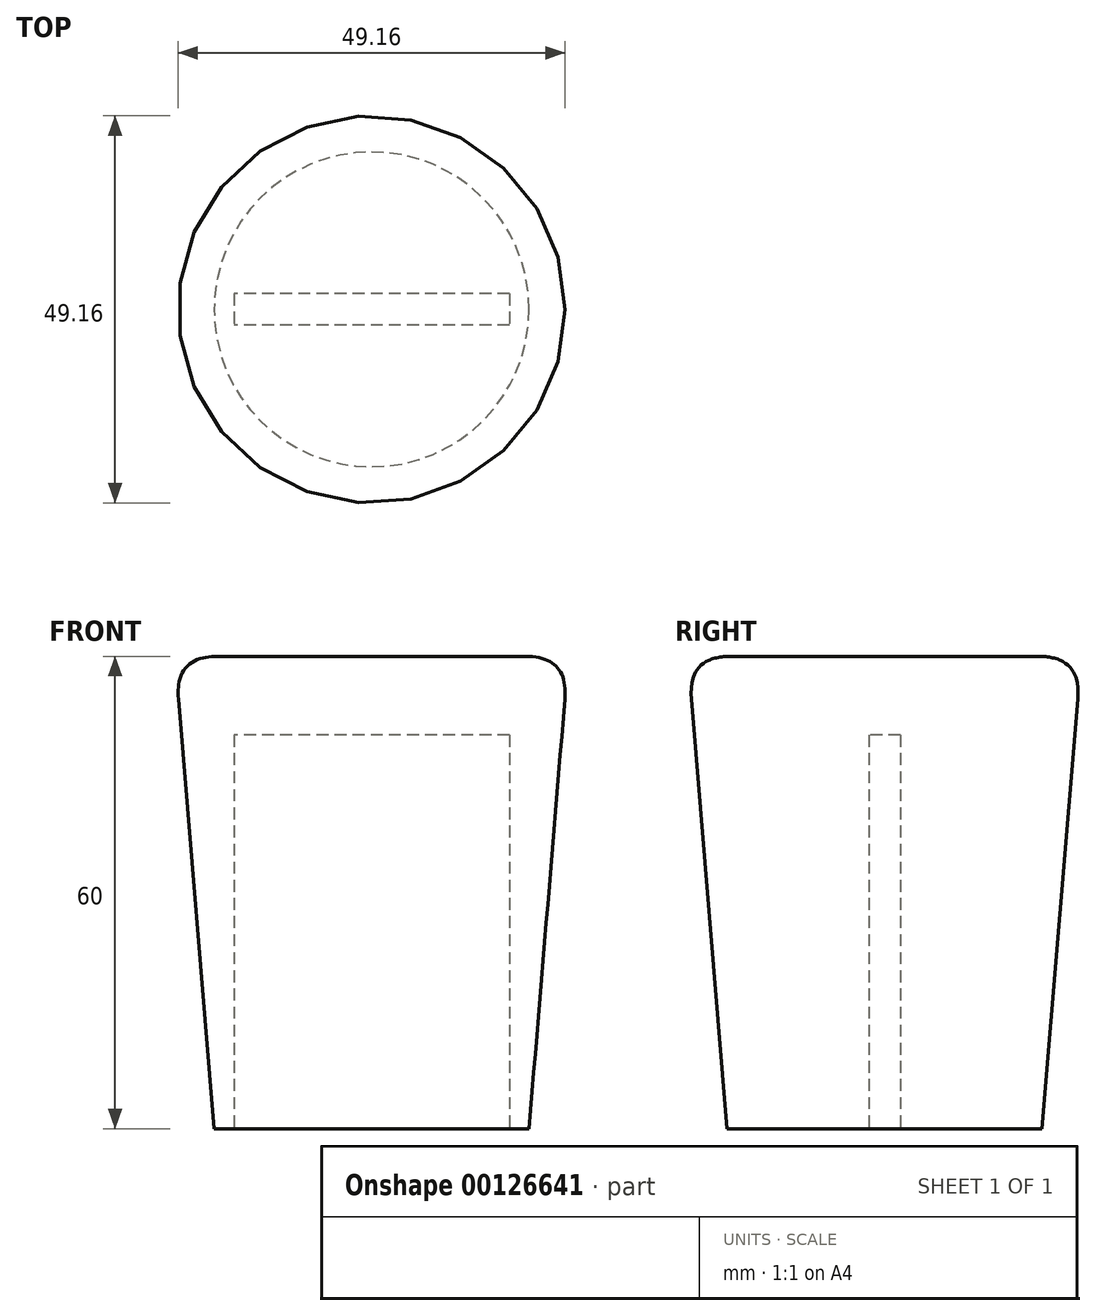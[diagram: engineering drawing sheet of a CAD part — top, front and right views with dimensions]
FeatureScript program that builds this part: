
annotation { "Feature Type Name" : "Feature", "Feature Type Description" : "" }
export const myFeature = defineFeature(function(context is Context, id is Id, definition is map)
    precondition{}
    {
        {
            var Q0;
            Q0=qCreatedBy(makeId("Front.planeOp"),FACE);
            var sketch = newSketch(context, id + "F0", { "sketchPlane" : qUnion([Q0])});
            skLineSegment(sketch, "E0", {"start": v(0, 0) * mm, "end": v(0, 60) * mm, "construction": true});
            skLineSegment(sketch, "E1", {"start": v(0, 0) * mm, "end": v(-20, 0) * mm});
            skLineSegment(sketch, "E2", {"start": v(0, 60) * mm, "end": v(-25, 60) * mm});
            skLineSegment(sketch, "E3", {"start": v(-25, 60) * mm, "end": v(-20, 0) * mm});
            skLineSegment(sketch, "E4", {"start": v(0, 60) * mm, "end": v(0, 0) * mm});
            skSolve(sketch);
        }
        {
            var Q0;
            Q0=qSketchRegion(id+"F0",true);
            var Q1;
            Q1=sQuery(id+"F0.wireOp",EDGE,"E4");
            revolve(context, id + "F1", {"entities" : qUnion([Q0]), "axis" : qUnion([Q1]), "revolveType" : RevolveType.FULL});
        }
        {
            var Q0;
            Q0=makeQuery(id+"F1.opRevolve","SWEPT_FACE",FACE,{"disambiguationData":[OSD([sQuery(id+"F0.wireOp",EDGE,"E1")])]});
            var sketch = newSketch(context, id + "F2", { "sketchPlane" : qUnion([Q0])});
            skLineSegment(sketch, "E5.bottom", {"start": v(17.5, -2) * mm, "end": v(-17.5, -2) * mm});
            skLineSegment(sketch, "E5.top", {"start": v(17.5, 2) * mm, "end": v(-17.5, 2) * mm});
            skLineSegment(sketch, "E5.left", {"start": v(17.5, -2) * mm, "end": v(17.5, 2) * mm});
            skLineSegment(sketch, "E5.right", {"start": v(-17.5, -2) * mm, "end": v(-17.5, 2) * mm});
            skPoint(sketch, "E5.middle", {"position": v(0, 0) * mm});
            skSolve(sketch);
        }
        {
            var Q0;
            Q0=qSketchRegion(id+"F2",true);
            extrude(context, id + "F3", {"entities" : qUnion([Q0]), "operationType" : NewBodyOperationType.REMOVE, "oppositeDirection" : true, "depth" : 50 * mm});
        }
        {
            var Q0;
            Q0=makeQuery(id+"F1.opRevolve","SWEPT_EDGE",EDGE,{"disambiguationData":[OSD([sQuery(id+"F0.wireOp",EDGE,"E2"),sQuery(id+"F0.wireOp",EDGE,"E3")])]});
            fillet(context, id + "F4", {"entities" : qUnion([Q0]), "radius" : 5 * mm, "tangentPropagation" : true, "rho" : 0.5, "crossSection" : FilletCrossSection.CONIC, "allowEdgeOverflow" : false});
        }
    });
